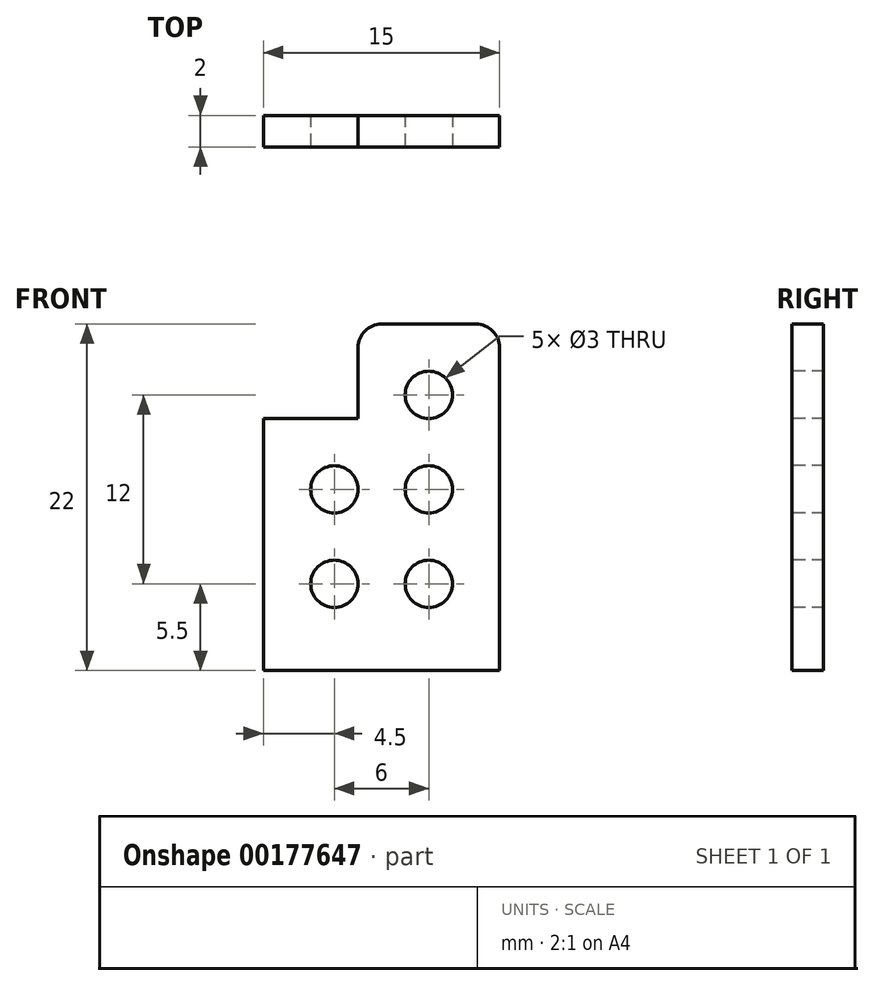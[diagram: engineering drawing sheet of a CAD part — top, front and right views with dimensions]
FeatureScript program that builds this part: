
annotation { "Feature Type Name" : "Feature", "Feature Type Description" : "" }
export const myFeature = defineFeature(function(context is Context, id is Id, definition is map)
    precondition{}
    {
        {
            var Q0;
            Q0=qCreatedBy(makeId("Front.planeOp"),FACE);
            var sketch = newSketch(context, id + "F0", { "sketchPlane" : qUnion([Q0])});
            skLineSegment(sketch, "E0.bottom", {"start": v(7.5, 7.5) * mm, "end": v(-7.5, 7.5) * mm});
            skLineSegment(sketch, "E0.top", {"start": v(7.5, -7.5) * mm, "end": v(-7.5, -7.5) * mm});
            skLineSegment(sketch, "E0.left", {"start": v(7.5, 7.5) * mm, "end": v(7.5, -7.5) * mm});
            skLineSegment(sketch, "E0.right", {"start": v(-7.5, 7.5) * mm, "end": v(-7.5, -7.5) * mm});
            skPoint(sketch, "E0.middle", {"position": v(0, 0) * mm});
            skSolve(sketch);
        }
        {
            var Q0;
            Q0=qSketchRegion(id+"F0",true);
            extrude(context, id + "F1", {"entities" : qUnion([Q0]), "depth" : 2 * mm});
        }
        {
            var Q0;
            Q0=makeQuery(id+"F1.opExtrude","CAP_FACE",FACE,{"disambiguationData":[OSD([sQuery(id+"F0.wireOp",EDGE,"E0.bottom"),sQuery(id+"F0.wireOp",EDGE,"E0.top"),sQuery(id+"F0.wireOp",EDGE,"E0.left"),sQuery(id+"F0.wireOp",EDGE,"E0.right")])],"isStart":false});
            var sketch = newSketch(context, id + "F2", { "sketchPlane" : qUnion([Q0])});
            skCircle(sketch, "E1", {"center": v(3, 3) * mm, "radius": 1.5 * mm});
            skCircle(sketch, "E2", {"center": v(-3, 3) * mm, "radius": 1.5 * mm});
            skCircle(sketch, "E3", {"center": v(-3, -3) * mm, "radius": 1.5 * mm});
            skCircle(sketch, "E4", {"center": v(3, -3) * mm, "radius": 1.5 * mm});
            skSolve(sketch);
        }
        {
            var Q0;
            Q0=qSketchRegion(id+"F2",true);
            extrude(context, id + "F3", {"entities" : qUnion([Q0]), "operationType" : NewBodyOperationType.REMOVE, "oppositeDirection" : true, "depth" : 25 * mm});
        }
        {
            var Q0;
            Q0=makeQuery(id+"F1.opExtrude","SWEPT_FACE",FACE,{"disambiguationData":[OSD([sQuery(id+"F0.wireOp",EDGE,"E0.bottom")])]});
            var sketch = newSketch(context, id + "F4", { "sketchPlane" : qUnion([Q0])});
            skLineSegment(sketch, "E5.bottom", {"start": v(7.5, 0) * mm, "end": v(-1.5, 0) * mm});
            skLineSegment(sketch, "E5.top", {"start": v(7.5, -2) * mm, "end": v(-1.5, -2) * mm});
            skLineSegment(sketch, "E5.left", {"start": v(7.5, 0) * mm, "end": v(7.5, -2) * mm});
            skLineSegment(sketch, "E5.right", {"start": v(-1.5, 0) * mm, "end": v(-1.5, -2) * mm});
            skSolve(sketch);
        }
        {
            var Q0;
            Q0=qSketchRegion(id+"F4",true);
            extrude(context, id + "F5", {"entities" : qUnion([Q0]), "operationType" : NewBodyOperationType.ADD, "depth" : 6 * mm});
        }
        {
            var Q0;
            Q0=makeQuery(id+"F5.boolean.opBoolean","MERGE",FACE,{"derivedFrom":[makeQuery(id+"F1.opExtrude","CAP_FACE",FACE,{"disambiguationData":[OSD([sQuery(id+"F0.wireOp",EDGE,"E0.bottom"),sQuery(id+"F0.wireOp",EDGE,"E0.top"),sQuery(id+"F0.wireOp",EDGE,"E0.left"),sQuery(id+"F0.wireOp",EDGE,"E0.right")])],"isStart":false}),makeQuery(id+"F5.opExtrude","SWEPT_FACE",FACE,{"disambiguationData":[OSD([sQuery(id+"F4.wireOp",EDGE,"E5.top")])]})]});
            var sketch = newSketch(context, id + "F6", { "sketchPlane" : qUnion([Q0])});
            skCircle(sketch, "E6", {"center": v(3, 9) * mm, "radius": 1.5 * mm});
            skSolve(sketch);
        }
        {
            var Q0;
            Q0=qSketchRegion(id+"F6",true);
            extrude(context, id + "F7", {"entities" : qUnion([Q0]), "operationType" : NewBodyOperationType.REMOVE, "oppositeDirection" : true, "depth" : 25 * mm});
        }
        {
            var Q0;
            Q0=makeQuery(id+"F5.opExtrude","CAP_EDGE",EDGE,{"disambiguationData":[OSD([sQuery(id+"F4.wireOp",EDGE,"E5.left")])],"isStart":false});
            var Q1;
            Q1=makeQuery(id+"F5.opExtrude","CAP_EDGE",EDGE,{"disambiguationData":[OSD([sQuery(id+"F4.wireOp",EDGE,"E5.right")])],"isStart":false});
            var Q2;
            Q2=makeQuery(id+"F5.opExtrude","CAP_EDGE",EDGE,{"disambiguationData":[OSD([sQuery(id+"F4.wireOp",EDGE,"E5.right")])],"isStart":true});
            fillet(context, id + "F8", {"entities" : qUnion([Q0, Q1, Q2]), "radius" : 1.5 * mm, "tangentPropagation" : true, "allowEdgeOverflow" : false});
        }
        {
            var Q0;
            Q0=makeQuery(id+"F1.opExtrude","SWEPT_FACE",FACE,{"disambiguationData":[OSD([sQuery(id+"F0.wireOp",EDGE,"E0.top")])]});
            var sketch = newSketch(context, id + "F9", { "sketchPlane" : qUnion([Q0])});
            skLineSegment(sketch, "E7.bottom", {"start": v(-7.5, 2) * mm, "end": v(7.5, 2) * mm});
            skLineSegment(sketch, "E7.top", {"start": v(-7.5, 0) * mm, "end": v(7.5, 0) * mm});
            skLineSegment(sketch, "E7.left", {"start": v(-7.5, 2) * mm, "end": v(-7.5, 0) * mm});
            skLineSegment(sketch, "E7.right", {"start": v(7.5, 2) * mm, "end": v(7.5, 0) * mm});
            skSolve(sketch);
        }
        {
            var Q0;
            Q0=qSketchRegion(id+"F9",true);
            extrude(context, id + "F10", {"entities" : qUnion([Q0]), "operationType" : NewBodyOperationType.ADD, "depth" : 1 * mm});
        }
    });
